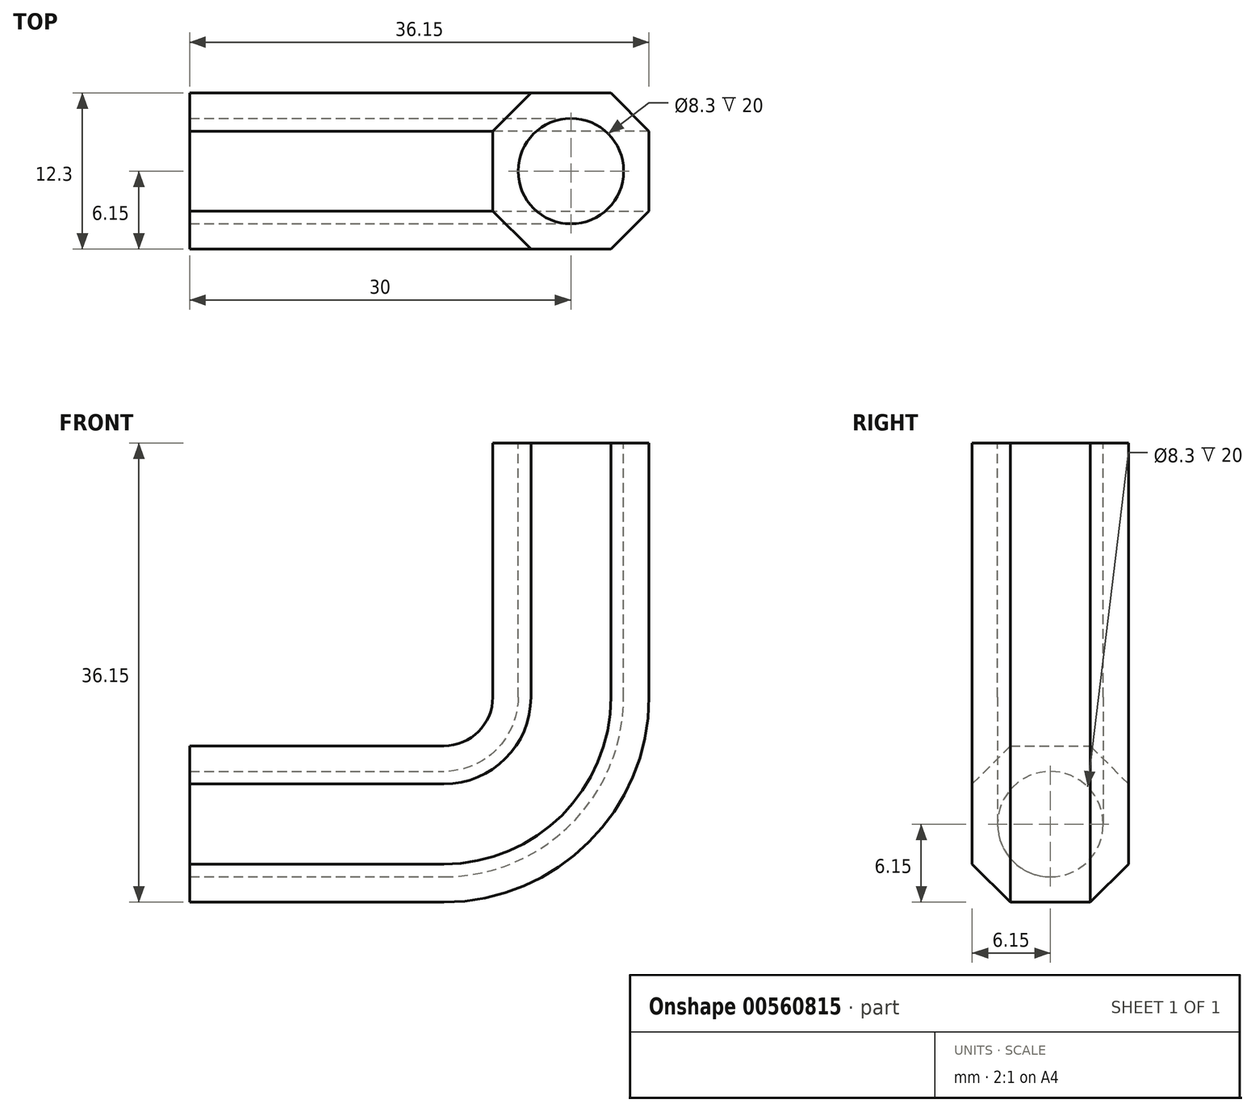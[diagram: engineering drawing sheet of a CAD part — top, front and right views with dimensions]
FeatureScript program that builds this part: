
annotation { "Feature Type Name" : "Feature", "Feature Type Description" : "" }
export const myFeature = defineFeature(function(context is Context, id is Id, definition is map)
    precondition{}
    {
        {
            var Q0;
            Q0=qCreatedBy(makeId("Front.planeOp"),FACE);
            var sketch = newSketch(context, id + "F0", { "sketchPlane" : qUnion([Q0])});
            skLineSegment(sketch, "E0", {"start": v(0, 0) * mm, "end": v(20, 0) * mm});
            skLineSegment(sketch, "E1", {"start": v(30, 10) * mm, "end": v(30, 30) * mm});
            skPoint(sketch, "E2.visualSharp", {"position": v(30, 0) * mm});
            skArc(sketch, "E2.filletArc", {"start": v(20, 0) * mm, "mid": v(27.07, 2.93) * mm, "end": v(30, 10) * mm});
            skSolve(sketch);
        }
        {
            var Q0;
            Q0=qCreatedBy(makeId("Right.planeOp"),FACE);
            var sketch = newSketch(context, id + "F1", { "sketchPlane" : qUnion([Q0])});
            skCircle(sketch, "E3", {"center": v(0, 0) * mm, "radius": 4.15 * mm});
            skCircle(sketch, "E4", {"center": v(0, 0) * mm, "radius": 6.15 * mm, "construction": true});
            skLineSegment(sketch, "E5.bottom", {"start": v(-6.15, 6.15) * mm, "end": v(6.15, 6.15) * mm});
            skLineSegment(sketch, "E5.top", {"start": v(-6.15, -6.15) * mm, "end": v(6.15, -6.15) * mm});
            skLineSegment(sketch, "E5.left", {"start": v(-6.15, 6.15) * mm, "end": v(-6.15, -6.15) * mm});
            skLineSegment(sketch, "E5.right", {"start": v(6.15, 6.15) * mm, "end": v(6.15, -6.15) * mm});
            skSolve(sketch);
        }
        {
            var Q0;
            Q0=makeQuery(id+"F1.imprint","IMPRINT",FACE,{"disambiguationData":[TD([[makeQuery(id+"F1.imprint","IMPRINT",EDGE,{"derivedFrom":sQuery(id+"F1.wireOp",EDGE,"E3")}),-1.0]])]});
            var Q1;
            Q1=sQuery(id+"F0.wireOp",EDGE,"E0");
            var Q2;
            Q2=sQuery(id+"F0.wireOp",EDGE,"E2.filletArc");
            var Q3;
            Q3=sQuery(id+"F0.wireOp",EDGE,"E1");
            sweep(context, id + "F2", {"profiles" : qUnion([Q0]), "path" : qUnion([Q1, Q2, Q3])});
        }
        {
            var Q0;
            Q0=makeQuery(id+"F2.opSweep","SWEPT_EDGE",EDGE,{"disambiguationData":[OSD([sQuery(id+"F0.wireOp",EDGE,"E1"),sQuery(id+"F1.wireOp",EDGE,"E5.bottom"),sQuery(id+"F1.wireOp",EDGE,"E5.left")])]});
            var Q1;
            Q1=makeQuery(id+"F2.opSweep","SWEPT_EDGE",EDGE,{"disambiguationData":[OSD([sQuery(id+"F0.wireOp",EDGE,"E1"),sQuery(id+"F1.wireOp",EDGE,"E5.top"),sQuery(id+"F1.wireOp",EDGE,"E5.left")])]});
            var Q2;
            Q2=makeQuery(id+"F2.opSweep","SWEPT_EDGE",EDGE,{"disambiguationData":[OSD([sQuery(id+"F0.wireOp",EDGE,"E1"),sQuery(id+"F1.wireOp",EDGE,"E5.top"),sQuery(id+"F1.wireOp",EDGE,"E5.right")])]});
            var Q3;
            Q3=makeQuery(id+"F2.opSweep","SWEPT_EDGE",EDGE,{"disambiguationData":[OSD([sQuery(id+"F0.wireOp",EDGE,"E1"),sQuery(id+"F1.wireOp",EDGE,"E5.bottom"),sQuery(id+"F1.wireOp",EDGE,"E5.right")])]});
            chamfer(context, id + "F3", {"entities" : qUnion([Q0, Q1, Q2, Q3]), "width" : 3 * mm, "tangentPropagation" : true});
        }
    });
